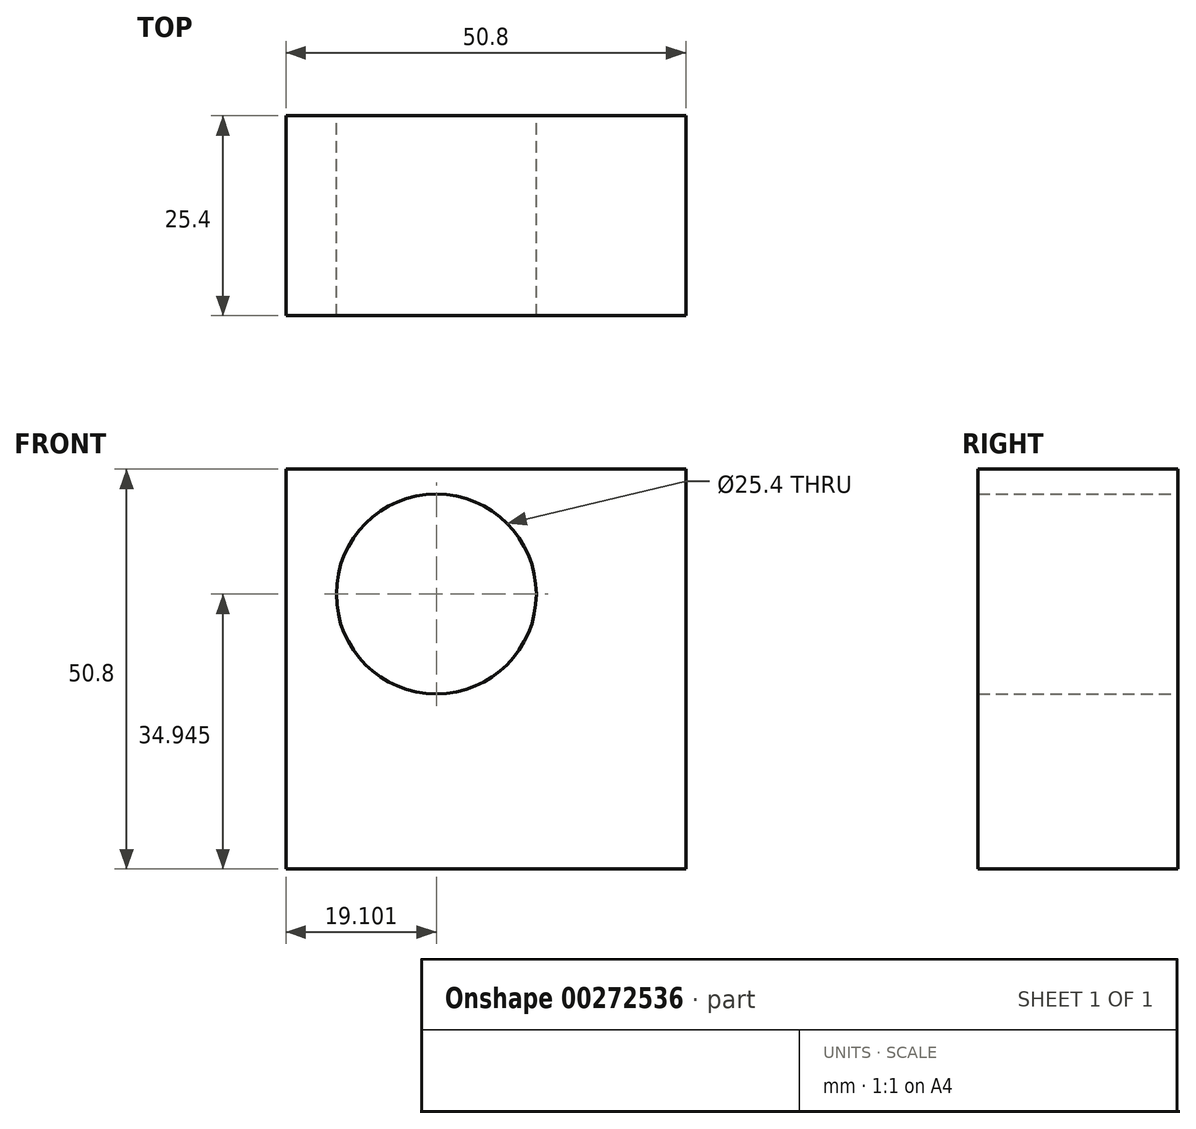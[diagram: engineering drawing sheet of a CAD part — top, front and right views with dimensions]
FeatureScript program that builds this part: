
annotation { "Feature Type Name" : "Feature", "Feature Type Description" : "" }
export const myFeature = defineFeature(function(context is Context, id is Id, definition is map)
    precondition{}
    {
        {
            var Q0;
            Q0=qCreatedBy(makeId("Front.planeOp"),FACE);
            var sketch = newSketch(context, id + "F0", { "sketchPlane" : qUnion([Q0])});
            skLineSegment(sketch, "E0.bottom", {"start": v(0, 0) * mm, "end": v(-50.8, 0) * mm});
            skLineSegment(sketch, "E0.top", {"start": v(0, 50.8) * mm, "end": v(-50.8, 50.8) * mm});
            skLineSegment(sketch, "E0.left", {"start": v(0, 0) * mm, "end": v(0, 50.8) * mm});
            skLineSegment(sketch, "E0.right", {"start": v(-50.8, 0) * mm, "end": v(-50.8, 50.8) * mm});
            skSolve(sketch);
        }
        {
            var Q0;
            Q0 = qSketchRegion(id + "F0", true);
            extrude(context, id + "F1", {"entities" : qUnion([Q0]), "depth" : 25.4 * mm});
        }
        {
            var Q0;
            Q0=qCreatedBy(makeId("Front.planeOp"),FACE);
            var sketch = newSketch(context, id + "F2", { "sketchPlane" : qUnion([Q0])});
            skCircle(sketch, "E1", {"center": v(-31.7, 34.94) * mm, "radius": 12.7 * mm});
            skCircle(sketch, "E2", {"center": v(-128.7, 74.1) * mm, "radius": 10.24 * mm});
            skSolve(sketch);
        }
        {
            var Q0;
            Q0=sQuery(id+"F2.wireOp",VERTEX,"E1.center");
            var Q1;
            Q1=makeQuery(id+"F1.opExtrude","SWEPT_BODY",BODY,{"disambiguationData":[OSD([sQuery(id+"F0.wireOp",EDGE,"E0.bottom"),sQuery(id+"F0.wireOp",EDGE,"E0.top"),sQuery(id+"F0.wireOp",EDGE,"E0.left"),sQuery(id+"F0.wireOp",EDGE,"E0.right")])]});
            hole(context, id + "F3", {"style" : HoleStyle.SIMPLE, "endStyle" : HoleEndStyle.THROUGH, "oppositeDirection" : true, "holeDiameter" : 25.4 * mm, "tappedDepth" : 12.7 * mm, "tapClearance" : 3, "locations" : qUnion([Q0]), "scope" : qUnion([Q1])});
        }
    });
